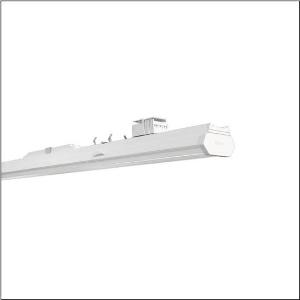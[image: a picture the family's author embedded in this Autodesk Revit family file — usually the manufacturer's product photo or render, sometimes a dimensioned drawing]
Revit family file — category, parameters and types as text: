
# Revit family: licross_r__11_protected_ho_51td12mn4f5m_c228
name_source: partatom
category: Lighting Fixtures
units: mm (PartAtom-declared; Revit-internal decimal feet)

## family parameters
Cut with Voids When Loaded = No
Host = Face
Light Source = No
Part Type = Normal
Room Calculation Point = No
Round Connector Dimension = Use Diameter
Shared = No

## types (1)
- --- (1 x LED, 15820 lm, 87.4 W, 4000K)
    Apparent Load = 87 VA
    CIE Flux Codes = 70 91 97 98 100
    Color Rendering = 80
    Color Temperature = 4000K
    Default Elevation = 1800 mm
    Description = Licross® 11 Protected HO, luminaire insert, of sheet steel, galvanised, coil coated, white, length: 1.500mm, width: 90mm, height: 101mm, LED rated luminous flux: 15.820lm, light colour: 840, control gear: ON/OFF Multilumen, with plug, 3-pole, with phase selection, mains connection: 220..240V, AC, 50/60Hz, rated input power: 87W, halogen-free wiring, primary light control with lens, of plastic, primary optical cover: cover, of PMMA, light emission: direct distribution, primary light characteristic: symmetric, protection rating (complete): IP54, insulation class (complete): insulation class I (protective earthing), certification: CE, ENEC, VDE, UKCA, protection symbol: D if used in an environment with non-conductive dust loads with corresponding accessories, impact resistance: IK06, permissible ambient temperature for indoor applications: -35..+35°C, corresponds to IFS (International Featured Standards) requirements for safety and quality in the food industry, reducing of maximum allowable ambient temperature of 5°C with ceiling mounting, LABS conformity tested according to VDMA 24364:2018-05, packaging unit: 1 piece
    Height = 92 mm
    Lamp = 1 x LED
    Lamp Light Flux = 15820 lm
    Lamp Power = 87.4 W
    Lamp count = 1
    Length = 1500 mm
    Luminous efficacy = 181 lm/W
    Manufacturer = Siteco
    ModVariant = No
    Model = 51TD12MN4F5M
    Mounting Place = Ceiling
    Mounting Type = Pendant
    Number of Poles = 1
    OnlyDefault = Yes
    Power Factor = 1
    Product Name = Licross® 11 Protected HO
    Product group = luminaire insert
    ProductGroupID = 901
    Protection Class = Protection class I
    Protection Degree = IP 54
    RLX_Detail_Level = 1
    RLX_Emergency_Light_Flux = 0 lm
    RLX_Emergency_Type = 0
    RLX_Emergency_Type_DB = No
    RlxData = <blob elided: 22001 chars, md5=f16b4404>
    Socket = socket
    Standby Power = 0 W
    System Light Flux = 15820 lm
    System Power = 87 W
    Type Comments = factory setting: luminous flux: 100 % | (A | C | E) | 203 mA
    Type Image = l_1256145.jpg
    URL = http://relux.com
    VarID = @adj_038189
    Voltage = 0 V
    Weight = 0.00 kg
    Width = 88 mm

## geometry (parser evidence)
native form markers: Blend x4, Sweep x11
no freeform markers — native parametric forms only
